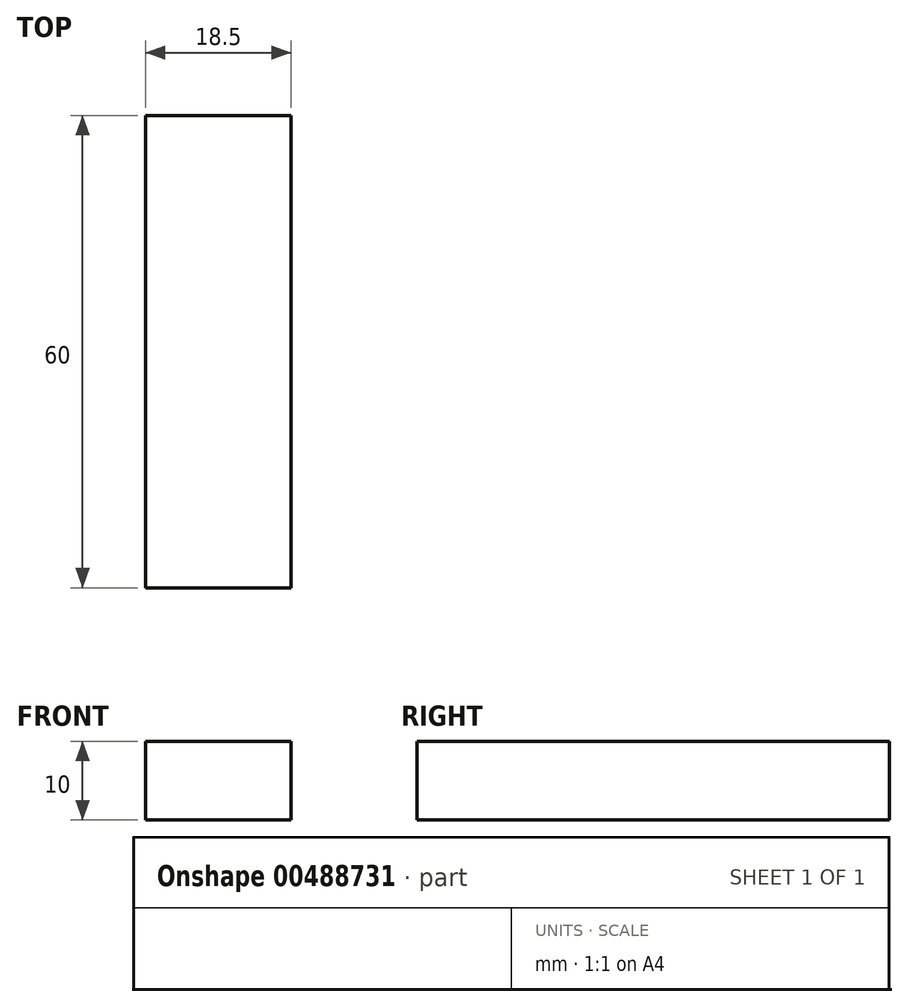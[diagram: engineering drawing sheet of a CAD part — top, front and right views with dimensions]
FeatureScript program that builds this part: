
annotation { "Feature Type Name" : "Feature", "Feature Type Description" : "" }
export const myFeature = defineFeature(function(context is Context, id is Id, definition is map)
    precondition{}
    {
        {
            var Q0;
            Q0=qCreatedBy(makeId("Top.planeOp"),FACE);
            var sketch = newSketch(context, id + "F0", { "sketchPlane" : qUnion([Q0])});
            skLineSegment(sketch, "E0.bottom", {"start": v(9.25, -30) * mm, "end": v(-9.25, -30) * mm});
            skLineSegment(sketch, "E0.top", {"start": v(9.25, 30) * mm, "end": v(-9.25, 30) * mm});
            skLineSegment(sketch, "E0.left", {"start": v(9.25, -30) * mm, "end": v(9.25, 30) * mm});
            skLineSegment(sketch, "E0.right", {"start": v(-9.25, -30) * mm, "end": v(-9.25, 30) * mm});
            skPoint(sketch, "E0.middle", {"position": v(0, 0) * mm});
            skSolve(sketch);
        }
        {
            var Q0;
            Q0=qSketchRegion(id+"F0",true);
            extrude(context, id + "F1", {"entities" : qUnion([Q0]), "endBound" : BoundingType.SYMMETRIC, "depth" : 10 * mm});
        }
    });
